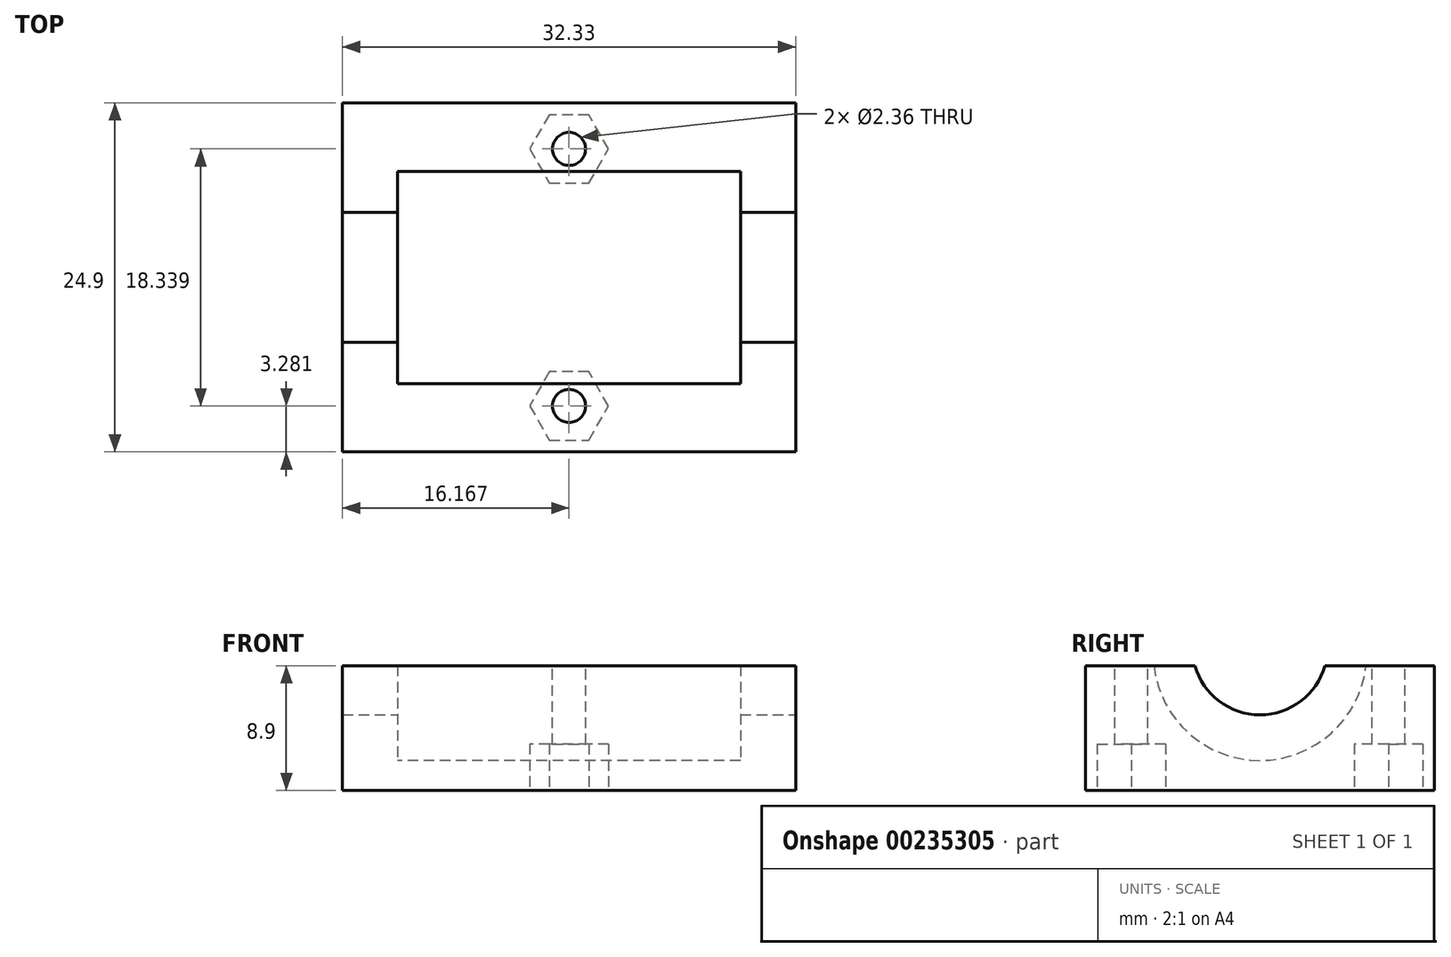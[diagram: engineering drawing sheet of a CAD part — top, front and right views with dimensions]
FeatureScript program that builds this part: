
annotation { "Feature Type Name" : "Feature", "Feature Type Description" : "" }
export const myFeature = defineFeature(function(context is Context, id is Id, definition is map)
    precondition{}
    {
        {
            var Q0;
            Q0=qCreatedBy(makeId("Right.planeOp"),FACE);
            var sketch = newSketch(context, id + "F0", { "sketchPlane" : qUnion([Q0])});
            skLineSegment(sketch, "E0.bottom", {"start": v(12.45, -4.44) * mm, "end": v(-12.45, -4.45) * mm});
            skLineSegment(sketch, "E0.top", {"start": v(12.45, 4.45) * mm, "end": v(-12.45, 4.44) * mm});
            skLineSegment(sketch, "E0.left", {"start": v(12.45, -4.44) * mm, "end": v(12.45, 4.45) * mm});
            skLineSegment(sketch, "E0.right", {"start": v(-12.45, -4.45) * mm, "end": v(-12.45, 4.44) * mm});
            skPoint(sketch, "E0.middle", {"position": v(0, 0) * mm});
            skSolve(sketch);
        }
        {
            var Q0;
            Q0=qSketchRegion(id+"F0",true);
            extrude(context, id + "F1", {"entities" : qUnion([Q0]), "depth" : 3.94 * mm});
        }
        {
            var Q0;
            Q0=makeQuery(id+"F1.opExtrude","CAP_FACE",FACE,{"disambiguationData":[OSD([sQuery(id+"F0.wireOp",EDGE,"E0.bottom"),sQuery(id+"F0.wireOp",EDGE,"E0.top"),sQuery(id+"F0.wireOp",EDGE,"E0.left"),sQuery(id+"F0.wireOp",EDGE,"E0.right")])],"isStart":false});
            var sketch = newSketch(context, id + "F2", { "sketchPlane" : qUnion([Q0])});
            skLineSegment(sketch, "E1.bottom", {"start": v(-12.45, 4.45) * mm, "end": v(-7.57, 4.45) * mm});
            skLineSegment(sketch, "E1.top", {"start": v(-12.45, -4.44) * mm, "end": v(12.45, -4.44) * mm});
            skLineSegment(sketch, "E1.left", {"start": v(-12.45, 4.44) * mm, "end": v(-12.45, -4.44) * mm});
            skLineSegment(sketch, "E1.right", {"start": v(12.45, 4.45) * mm, "end": v(12.45, -4.44) * mm});
            skLineSegment(sketch, "E2.trimOffspring", {"start": v(7.57, 4.45) * mm, "end": v(12.45, 4.45) * mm});
            skArc(sketch, "E3", {"start": v(-7.57, 4.45) * mm, "mid": v(0, -2.31) * mm, "end": v(7.57, 4.45) * mm});
            skSolve(sketch);
        }
        {
            var Q0;
            Q0=qSketchRegion(id+"F2",true);
            extrude(context, id + "F3", {"entities" : qUnion([Q0]), "operationType" : NewBodyOperationType.ADD, "depth" : 24.46 * mm});
        }
        {
            var Q0;
            Q0=makeQuery(id+"F3.opExtrude","CAP_FACE",FACE,{"disambiguationData":[OSD([sQuery(id+"F2.wireOp",EDGE,"E1.bottom"),sQuery(id+"F2.wireOp",EDGE,"E1.top"),sQuery(id+"F2.wireOp",EDGE,"E1.left"),sQuery(id+"F2.wireOp",EDGE,"E1.right"),sQuery(id+"F2.wireOp",EDGE,"TYnsB8ya-WYle-G6CB-24iZ-T6w1Zh2Edi8s"),sQuery(id+"F2.wireOp",EDGE,"8Qk2cRYJ-O90g-r4A9-VzlO-tEoDoWINZZq2"),sQuery(id+"F2.wireOp",EDGE,"Tx2M3oyi-r9D9-EWBA-TI7Q-Y03CfVB0JWJh"),sQuery(id+"F2.wireOp",EDGE,"E2.trimOffspring")])],"isStart":false});
            var sketch = newSketch(context, id + "F4", { "sketchPlane" : qUnion([Q0])});
            skLineSegment(sketch, "E4.bottom", {"start": v(-12.45, 4.44) * mm, "end": v(12.45, 4.44) * mm});
            skLineSegment(sketch, "E4.top", {"start": v(-12.45, -4.44) * mm, "end": v(12.45, -4.44) * mm});
            skLineSegment(sketch, "E4.left", {"start": v(-12.45, 4.44) * mm, "end": v(-12.45, -4.44) * mm});
            skLineSegment(sketch, "E4.right", {"start": v(12.45, 4.44) * mm, "end": v(12.45, -4.44) * mm});
            skSolve(sketch);
        }
        {
            var Q0;
            Q0=qSketchRegion(id+"F4",true);
            extrude(context, id + "F5", {"entities" : qUnion([Q0]), "operationType" : NewBodyOperationType.ADD, "depth" : 3.94 * mm});
        }
        {
            var Q0;
            Q0=makeQuery(id+"F5.opExtrude","CAP_FACE",FACE,{"disambiguationData":[OSD([sQuery(id+"F4.wireOp",EDGE,"E4.bottom"),sQuery(id+"F4.wireOp",EDGE,"E4.top"),sQuery(id+"F4.wireOp",EDGE,"E4.left"),sQuery(id+"F4.wireOp",EDGE,"E4.right")])],"isStart":false});
            var sketch = newSketch(context, id + "F6", { "sketchPlane" : qUnion([Q0])});
            skCircle(sketch, "E5", {"center": v(0, 5.77) * mm, "radius": 4.83 * mm});
            skPoint(sketch, "E5.centerSnap0", {"position": v(0, 4.45) * mm});
            skSolve(sketch);
        }
        {
            var Q0;
            {var subQ0=sQuery(id+"F6.wireOp",EDGE,"E5");var subQ1=makeQuery(id+"F5.opExtrude","CAP_EDGE",EDGE,{"disambiguationData":[OSD([sQuery(id+"F4.wireOp",EDGE,"E4.bottom")])],"isStart":false});var subQ2=makeQuery(id+"F6.imprint","INTERSECT",VERTEX,{"disambiguationData":[OD(0.0)],"derivedFrom":[subQ1,subQ0]});Q0=makeQuery(id+"F6.imprint","IMPRINT",FACE,{"disambiguationData":[TD([[makeQuery(id+"F6.imprint","IMPRINT",EDGE,{"disambiguationData":[TD([[subQ2,1.0]])],"derivedFrom":subQ0}),1.0]])]});}
            extrude(context, id + "F7", {"entities" : qUnion([Q0]), "operationType" : NewBodyOperationType.REMOVE, "endBound" : BoundingType.THROUGH_ALL, "oppositeDirection" : true, "depth" : 25.4 * mm});
        }
        {
            var Q0;
            {var subQ3=sQuery(id+"F4.wireOp",EDGE,"E4.bottom");var subQ4=sQuery(id+"F0.wireOp",EDGE,"E0.right");var subQ6=sQuery(id+"F0.wireOp",EDGE,"E0.top");Q0=makeQuery(id+"F7.boolean.opBoolean","SPLIT",FACE,{"disambiguationData":[TD([makeQuery(id+"F1.opExtrude","SWEPT_FACE",FACE,{"disambiguationData":[OSD([subQ4])]})])],"derivedFrom":makeQuery(id+"F5.boolean.opBoolean","MERGE",FACE,{"derivedFrom":[makeQuery(id+"F3.boolean.opBoolean","MERGE",FACE,{"derivedFrom":[makeQuery(id+"F1.opExtrude","SWEPT_FACE",FACE,{"disambiguationData":[OSD([subQ6])]}),makeQuery(id+"F3.opExtrude","SWEPT_FACE",FACE,{"disambiguationData":[OSD([sQuery(id+"F2.wireOp",EDGE,"E1.bottom")])]}),makeQuery(id+"F3.opExtrude","SWEPT_FACE",FACE,{"disambiguationData":[OSD([sQuery(id+"F2.wireOp",EDGE,"E2.trimOffspring")])]})]}),makeQuery(id+"F5.opExtrude","SWEPT_FACE",FACE,{"disambiguationData":[OSD([subQ3])]})]})});}
            var sketch = newSketch(context, id + "F8", { "sketchPlane" : qUnion([Q0])});
            skCircle(sketch, "E6", {"center": v(16.17, -9.17) * mm, "radius": 1.18 * mm});
            skCircle(sketch, "E7", {"center": v(16.17, 9.17) * mm, "radius": 1.18 * mm});
            skSolve(sketch);
        }
        {
            var Q0;
            Q0=qSketchRegion(id+"F8",true);
            extrude(context, id + "F9", {"entities" : qUnion([Q0]), "operationType" : NewBodyOperationType.REMOVE, "endBound" : BoundingType.THROUGH_ALL, "oppositeDirection" : true, "depth" : 25.4 * mm});
        }
        {
            var Q0;
            Q0=makeQuery(id+"F5.boolean.opBoolean","MERGE",FACE,{"derivedFrom":[makeQuery(id+"F3.boolean.opBoolean","MERGE",FACE,{"derivedFrom":[makeQuery(id+"F1.opExtrude","SWEPT_FACE",FACE,{"disambiguationData":[OSD([sQuery(id+"F0.wireOp",EDGE,"E0.bottom")])]}),makeQuery(id+"F3.opExtrude","SWEPT_FACE",FACE,{"disambiguationData":[OSD([sQuery(id+"F2.wireOp",EDGE,"E1.top")])]})]}),makeQuery(id+"F5.opExtrude","SWEPT_FACE",FACE,{"disambiguationData":[OSD([sQuery(id+"F4.wireOp",EDGE,"E4.top")])]})]});
            var sketch = newSketch(context, id + "F10", { "sketchPlane" : qUnion([Q0])});
            skCircle(sketch, "E8.cCircle", {"center": v(16.17, -9.17) * mm, "radius": 2.44 * mm, "construction": true});
            skLineSegment(sketch, "E8.0", {"start": v(13.35, -9.17) * mm, "end": v(14.76, -6.73) * mm});
            skLineSegment(sketch, "E8.1", {"start": v(14.76, -6.73) * mm, "end": v(17.57, -6.73) * mm});
            skLineSegment(sketch, "E8.2", {"start": v(17.57, -6.73) * mm, "end": v(18.98, -9.17) * mm});
            skLineSegment(sketch, "E8.3", {"start": v(18.98, -9.17) * mm, "end": v(17.57, -11.6) * mm});
            skLineSegment(sketch, "E8.4", {"start": v(17.57, -11.6) * mm, "end": v(14.76, -11.6) * mm});
            skLineSegment(sketch, "E8.5", {"start": v(14.76, -11.6) * mm, "end": v(13.35, -9.17) * mm});
            skPoint(sketch, "E8.0.midPoint", {"position": v(14.06, -7.95) * mm});
            skCircle(sketch, "E9.cCircle", {"center": v(16.17, 9.17) * mm, "radius": 2.44 * mm, "construction": true});
            skLineSegment(sketch, "E9.0", {"start": v(14.76, 6.73) * mm, "end": v(13.35, 9.17) * mm});
            skLineSegment(sketch, "E9.1", {"start": v(13.35, 9.17) * mm, "end": v(14.76, 11.6) * mm});
            skLineSegment(sketch, "E9.2", {"start": v(14.76, 11.6) * mm, "end": v(17.57, 11.6) * mm});
            skLineSegment(sketch, "E9.3", {"start": v(17.57, 11.6) * mm, "end": v(18.98, 9.17) * mm});
            skLineSegment(sketch, "E9.4", {"start": v(18.98, 9.17) * mm, "end": v(17.57, 6.73) * mm});
            skLineSegment(sketch, "E9.5", {"start": v(17.57, 6.73) * mm, "end": v(14.76, 6.73) * mm});
            skPoint(sketch, "E9.0.midPoint", {"position": v(14.06, 7.95) * mm});
            skSolve(sketch);
        }
        {
            var Q0;
            Q0=qSketchRegion(id+"F10",true);
            extrude(context, id + "F11", {"entities" : qUnion([Q0]), "operationType" : NewBodyOperationType.REMOVE, "oppositeDirection" : true, "depth" : 3.3 * mm});
        }
    });
